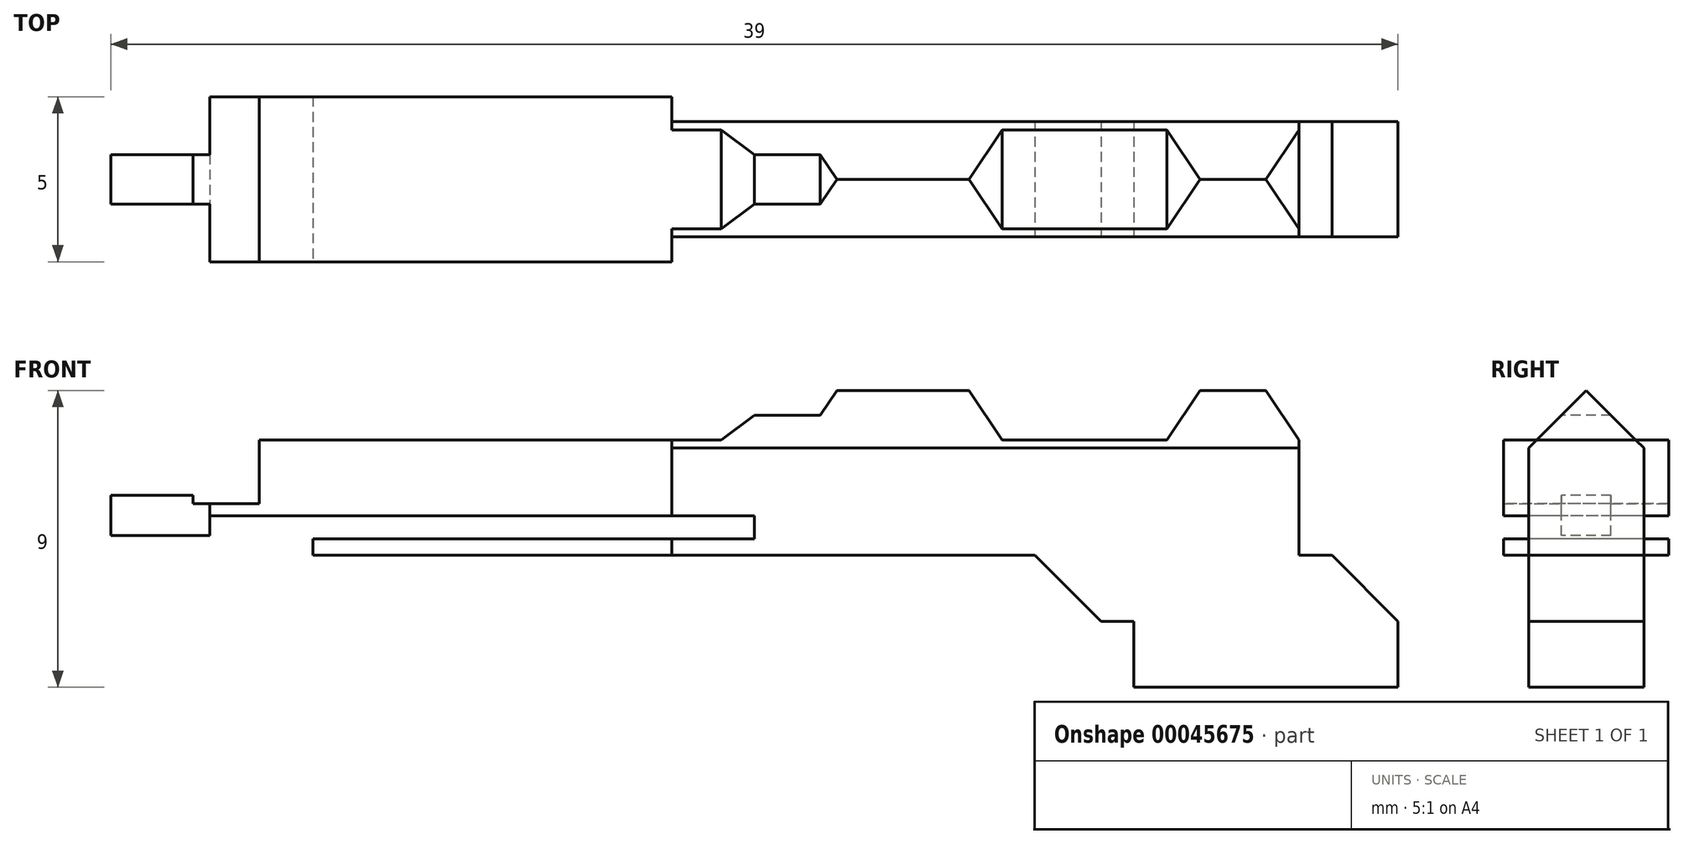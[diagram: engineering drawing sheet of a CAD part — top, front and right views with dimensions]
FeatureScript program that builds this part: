
annotation { "Feature Type Name" : "Feature", "Feature Type Description" : "" }
export const myFeature = defineFeature(function(context is Context, id is Id, definition is map)
    precondition{}
    {
        {
            var Q0;
            Q0=qCreatedBy(makeId("Top.planeOp"),FACE);
            var sketch = newSketch(context, id + "F0", { "sketchPlane" : qUnion([Q0])});
            skLineSegment(sketch, "E0.bottom", {"start": v(-9.8, 2.5) * mm, "end": v(4.2, 2.5) * mm});
            skLineSegment(sketch, "E0.top", {"start": v(-9.8, -2.5) * mm, "end": v(4.2, -2.5) * mm});
            skLineSegment(sketch, "E0.left", {"start": v(-9.8, 2.5) * mm, "end": v(-9.8, -2.5) * mm});
            skLineSegment(sketch, "E0.right", {"start": v(4.2, 2.5) * mm, "end": v(4.2, 1.75) * mm});
            skLineSegment(sketch, "E1.bottom", {"start": v(4.2, 1.75) * mm, "end": v(26.2, 1.75) * mm});
            skLineSegment(sketch, "E1.top", {"start": v(4.2, -1.75) * mm, "end": v(26.2, -1.75) * mm});
            skLineSegment(sketch, "E1.right", {"start": v(26.2, 1.75) * mm, "end": v(26.2, -1.75) * mm});
            skLineSegment(sketch, "E2.bottom", {"start": v(18.2, 1.75) * mm, "end": v(26.2, 1.75) * mm});
            skLineSegment(sketch, "E2.top", {"start": v(18.2, -1.75) * mm, "end": v(26.2, -1.75) * mm});
            skLineSegment(sketch, "E2.right", {"start": v(18.2, 1.75) * mm, "end": v(18.2, -1.75) * mm});
            skLineSegment(sketch, "E3.bottom", {"start": v(15.2, 1.75) * mm, "end": v(18.2, 1.75) * mm});
            skLineSegment(sketch, "E3.top", {"start": v(15.2, -1.75) * mm, "end": v(18.2, -1.75) * mm});
            skLineSegment(sketch, "E3.right", {"start": v(15.2, 1.75) * mm, "end": v(15.2, -1.75) * mm});
            skLineSegment(sketch, "E4.trimOffspring", {"start": v(4.2, -1.75) * mm, "end": v(4.2, -2.5) * mm});
            skLineSegment(sketch, "E5.bottom", {"start": v(15.2, 1.75) * mm, "end": v(17.2, 1.75) * mm});
            skLineSegment(sketch, "E5.top", {"start": v(15.2, -1.75) * mm, "end": v(17.2, -1.75) * mm});
            skLineSegment(sketch, "E5.right", {"start": v(17.2, 1.75) * mm, "end": v(17.2, -1.75) * mm});
            skLineSegment(sketch, "E6", {"start": v(-9.8, 0) * mm, "end": v(17.2, 0) * mm, "construction": true});
            skLineSegment(sketch, "E7.bottom", {"start": v(-9.8, 0.75) * mm, "end": v(-12.8, 0.75) * mm});
            skLineSegment(sketch, "E7.top", {"start": v(-9.8, -0.75) * mm, "end": v(-12.8, -0.75) * mm});
            skLineSegment(sketch, "E7.left", {"start": v(-9.8, 0.75) * mm, "end": v(-9.8, -0.75) * mm});
            skLineSegment(sketch, "E7.right", {"start": v(-12.8, 0.75) * mm, "end": v(-12.8, -0.75) * mm});
            skLineSegment(sketch, "E8", {"start": v(-12.8, 0) * mm, "end": v(-9.8, 0) * mm, "construction": true});
            skSolve(sketch);
        }
        {
            var Q0;
            Q0 = qSketchRegion(id + "F0", true);
            extrude(context, id + "F1", {"entities" : qUnion([Q0]), "oppositeDirection" : true, "depth" : 9 * mm});
        }
        {
            var Q0;
            Q0=makeQuery(id+"F1.opExtrude","SWEPT_FACE",FACE,{"disambiguationData":[OSD([sQuery(id+"F0.wireOp",EDGE,"E0.bottom")])]});
            cPlane(context, id + "F2", {"entities" : qUnion([Q0]), "cplaneType" : CPlaneType.OFFSET, "offset" : 0 * mm, "width" : 150 * mm, "height" : 150 * mm});
        }
        {
            var Q0;
            Q0=qCreatedBy(id+"F2.planeOp",FACE);
            var sketch = newSketch(context, id + "F3", { "sketchPlane" : qUnion([Q0])});
            skLineSegment(sketch, "E9.0.0", {"start": v(-26.2, 0) * mm, "end": v(-4.2, 0) * mm});
            skLineSegment(sketch, "E9.0.2", {"start": v(-4.2, -9) * mm, "end": v(-26.2, -9) * mm});
            skLineSegment(sketch, "E9.0.3", {"start": v(-26.2, -9) * mm, "end": v(-26.2, 0) * mm});
            skLineSegment(sketch, "E10.0.0", {"start": v(-4.2, 0) * mm, "end": v(9.8, 0) * mm});
            skLineSegment(sketch, "E10.0.2", {"start": v(9.8, -9) * mm, "end": v(-4.2, -9) * mm});
            skLineSegment(sketch, "E11.0.0", {"start": v(9.8, 0) * mm, "end": v(12.8, 0) * mm});
            skLineSegment(sketch, "E11.0.1", {"start": v(12.8, 0) * mm, "end": v(12.8, -9) * mm});
            skLineSegment(sketch, "E11.0.2", {"start": v(12.8, -9) * mm, "end": v(9.8, -9) * mm});
            skLineSegment(sketch, "E12", {"start": v(-24.2, 0) * mm, "end": v(-24.2, -9) * mm, "construction": true});
            skLineSegment(sketch, "E13", {"start": v(-23.2, 0) * mm, "end": v(-23.2, -9) * mm, "construction": true});
            skLineSegment(sketch, "E14", {"start": v(-22.2, 0) * mm, "end": v(-22.2, -9) * mm, "construction": true});
            skLineSegment(sketch, "E15", {"start": v(-20.2, 0) * mm, "end": v(-20.2, -9) * mm, "construction": true});
            skLineSegment(sketch, "E16", {"start": v(-19.2, 0) * mm, "end": v(-19.2, -9) * mm, "construction": true});
            skLineSegment(sketch, "E17", {"start": v(-18.2, 0) * mm, "end": v(-18.2, -9) * mm, "construction": true});
            skLineSegment(sketch, "E18", {"start": v(-18.2, -7) * mm, "end": v(-26.2, -7) * mm, "construction": true});
            skLineSegment(sketch, "E19", {"start": v(-18.2, -5) * mm, "end": v(-26.2, -5) * mm, "construction": true});
            skLineSegment(sketch, "E20", {"start": v(-18.2, -1.5) * mm, "end": v(-26.2, -1.5) * mm, "construction": true});
            skLineSegment(sketch, "E21", {"start": v(-26.2, -7) * mm, "end": v(-24.2, -5) * mm});
            skLineSegment(sketch, "E22", {"start": v(-24.2, -5) * mm, "end": v(-23.2, -5) * mm});
            skLineSegment(sketch, "E23", {"start": v(-23.2, -5) * mm, "end": v(-23.2, -1.5) * mm});
            skLineSegment(sketch, "E24", {"start": v(-23.2, -1.5) * mm, "end": v(-22.2, 0) * mm});
            skLineSegment(sketch, "E25", {"start": v(-20.2, 0) * mm, "end": v(-22.2, 0) * mm});
            skLineSegment(sketch, "E26", {"start": v(-20.2, 0) * mm, "end": v(-19.2, -1.5) * mm});
            skLineSegment(sketch, "E27", {"start": v(-19.2, -1.5) * mm, "end": v(-18.2, -1.5) * mm});
            skSolve(sketch);
        }
        {
            var Q0;
            Q0=qCreatedBy(id+"F2.planeOp",FACE);
            var sketch = newSketch(context, id + "F4", { "sketchPlane" : qUnion([Q0])});
            skLineSegment(sketch, "E28.0", {"start": v(-24.2, -5) * mm, "end": v(-23.2, -5) * mm});
            skLineSegment(sketch, "E29.0", {"start": v(-23.2, -5) * mm, "end": v(-23.2, -1.5) * mm});
            skLineSegment(sketch, "E30.0", {"start": v(-26.2, -7) * mm, "end": v(-24.2, -5) * mm});
            skLineSegment(sketch, "E31.0", {"start": v(-23.2, -1.5) * mm, "end": v(-22.2, 0) * mm});
            skLineSegment(sketch, "E32.0", {"start": v(-20.2, 0) * mm, "end": v(-22.2, 0) * mm});
            skLineSegment(sketch, "E33.0", {"start": v(-20.2, 0) * mm, "end": v(-19.2, -1.5) * mm});
            skLineSegment(sketch, "E34.0", {"start": v(-19.2, -1.5) * mm, "end": v(-18.2, -1.5) * mm});
            skLineSegment(sketch, "E35", {"start": v(-18.2, -1.5) * mm, "end": v(-18.2, 0) * mm});
            skLineSegment(sketch, "E36", {"start": v(-18.2, 0) * mm, "end": v(-20.2, 0) * mm});
            skLineSegment(sketch, "E37.0", {"start": v(-26.2, -7) * mm, "end": v(-26.2, 0) * mm});
            skLineSegment(sketch, "E38.0", {"start": v(-26.2, 0) * mm, "end": v(-22.2, 0) * mm});
            skPoint(sketch, "E39.orphan", {"position": v(-4.2, 0) * mm});
            skLineSegment(sketch, "E40.trimOffspring", {"start": v(-20.2, 0) * mm, "end": v(-18.2, 0) * mm});
            skPoint(sketch, "E41.orphan", {"position": v(-26.2, -9) * mm});
            skSolve(sketch);
        }
        {
            var Q0;
            Q0 = qSketchRegion(id + "F4", true);
            extrude(context, id + "F5", {"entities" : qUnion([Q0]), "operationType" : NewBodyOperationType.REMOVE, "oppositeDirection" : true, "depth" : 25 * mm});
        }
        {
            var Q0;
            Q0=makeQuery(id+"F1.opExtrude","SWEPT_FACE",FACE,{"disambiguationData":[OSD([sQuery(id+"F0.wireOp",EDGE,"E1.top"),sQuery(id+"F0.wireOp",EDGE,"E2.top"),sQuery(id+"F0.wireOp",EDGE,"E3.top"),sQuery(id+"F0.wireOp",EDGE,"E5.top")])]});
            var sketch = newSketch(context, id + "F6", { "sketchPlane" : qUnion([Q0])});
            skLineSegment(sketch, "E42.0.0", {"start": v(20.2, 0) * mm, "end": v(19.2, -1.5) * mm, "construction": true});
            skLineSegment(sketch, "E42.0.1", {"start": v(19.2, -1.5) * mm, "end": v(18.2, -1.5) * mm, "construction": true});
            skLineSegment(sketch, "E42.0.2", {"start": v(18.2, -1.5) * mm, "end": v(18.2, 0) * mm, "construction": true});
            skLineSegment(sketch, "E42.0.3", {"start": v(18.2, 0) * mm, "end": v(4.2, 0) * mm, "construction": true});
            skLineSegment(sketch, "E42.0.4", {"start": v(4.2, 0) * mm, "end": v(4.2, -9) * mm, "construction": true});
            skLineSegment(sketch, "E42.0.5", {"start": v(4.2, -9) * mm, "end": v(26.2, -9) * mm, "construction": true});
            skLineSegment(sketch, "E42.0.6", {"start": v(26.2, -9) * mm, "end": v(26.2, -7) * mm, "construction": true});
            skLineSegment(sketch, "E42.0.7", {"start": v(26.2, -7) * mm, "end": v(24.2, -5) * mm, "construction": true});
            skLineSegment(sketch, "E42.0.8", {"start": v(24.2, -5) * mm, "end": v(23.2, -5) * mm, "construction": true});
            skLineSegment(sketch, "E42.0.9", {"start": v(23.2, -5) * mm, "end": v(23.2, -1.5) * mm, "construction": true});
            skLineSegment(sketch, "E42.0.10", {"start": v(23.2, -1.5) * mm, "end": v(22.2, 0) * mm, "construction": true});
            skLineSegment(sketch, "E42.0.11", {"start": v(22.2, 0) * mm, "end": v(20.2, 0) * mm, "construction": true});
            skLineSegment(sketch, "E43", {"start": v(18.2, 0) * mm, "end": v(18.2, -9) * mm, "construction": true});
            skLineSegment(sketch, "E44", {"start": v(17.2, 0) * mm, "end": v(17.2, -9) * mm, "construction": true});
            skLineSegment(sketch, "E45", {"start": v(15.2, 0) * mm, "end": v(15.2, -9) * mm, "construction": true});
            skLineSegment(sketch, "E46", {"start": v(14.2, 0) * mm, "end": v(14.2, -9) * mm, "construction": true});
            skLineSegment(sketch, "E47", {"start": v(13.2, 0) * mm, "end": v(13.2, -9) * mm, "construction": true});
            skLineSegment(sketch, "E48", {"start": v(9.2, 0) * mm, "end": v(9.2, -9) * mm, "construction": true});
            skLineSegment(sketch, "E49", {"start": v(5.7, 0) * mm, "end": v(5.7, -9) * mm, "construction": true});
            skLineSegment(sketch, "E50", {"start": v(6.7, 0) * mm, "end": v(6.7, -9) * mm, "construction": true});
            skLineSegment(sketch, "E51", {"start": v(8.7, 0) * mm, "end": v(8.7, -9) * mm, "construction": true});
            skLineSegment(sketch, "E52", {"start": v(18.2, -1.5) * mm, "end": v(4.2, -1.5) * mm, "construction": true});
            skLineSegment(sketch, "E53", {"start": v(18.2, -3.5) * mm, "end": v(4.2, -3.5) * mm, "construction": true});
            skLineSegment(sketch, "E54", {"start": v(18.2, -5) * mm, "end": v(4.2, -5) * mm, "construction": true});
            skLineSegment(sketch, "E55", {"start": v(18.2, -7) * mm, "end": v(4.2, -7) * mm, "construction": true});
            skLineSegment(sketch, "E56", {"start": v(18.2, -9) * mm, "end": v(18.2, -7) * mm});
            skLineSegment(sketch, "E57", {"start": v(18.2, -7) * mm, "end": v(17.2, -7) * mm});
            skLineSegment(sketch, "E58", {"start": v(17.2, -7) * mm, "end": v(15.2, -5) * mm});
            skLineSegment(sketch, "E59", {"start": v(4.2, -5) * mm, "end": v(15.2, -5) * mm});
            skLineSegment(sketch, "E60", {"start": v(4.2, -5) * mm, "end": v(4.2, -9) * mm});
            skLineSegment(sketch, "E61", {"start": v(4.2, -9) * mm, "end": v(18.2, -9) * mm});
            skLineSegment(sketch, "E62", {"start": v(18.2, -1.5) * mm, "end": v(15.2, -1.5) * mm});
            skLineSegment(sketch, "E63", {"start": v(14.2, -1.5) * mm, "end": v(15.2, -1.5) * mm});
            skLineSegment(sketch, "E64", {"start": v(14.2, -1.5) * mm, "end": v(13.2, 0) * mm});
            skLineSegment(sketch, "E65", {"start": v(13.2, 0) * mm, "end": v(9.2, 0) * mm});
            skLineSegment(sketch, "E66", {"start": v(4.2, 0) * mm, "end": v(18.2, 0) * mm});
            skLineSegment(sketch, "E67", {"start": v(18.2, 0) * mm, "end": v(18.2, -1.5) * mm});
            skLineSegment(sketch, "E68", {"start": v(4.2, -1.5) * mm, "end": v(4.2, -2.5) * mm});
            skPoint(sketch, "E69.startSnap0", {"position": v(4.2, -2.5) * mm});
            skPoint(sketch, "E70.start.orphan", {"position": v(5.7, -2.5) * mm});
            skLineSegment(sketch, "E71", {"start": v(4.2, -1.5) * mm, "end": v(4.2, 0) * mm});
            skLineSegment(sketch, "E72", {"start": v(4.2, -0.75) * mm, "end": v(18.2, -0.75) * mm, "construction": true});
            skLineSegment(sketch, "E73", {"start": v(9.2, 0) * mm, "end": v(8.7, -0.75) * mm});
            skLineSegment(sketch, "E74", {"start": v(8.7, -0.75) * mm, "end": v(6.7, -0.75) * mm});
            skLineSegment(sketch, "E75", {"start": v(6.7, -0.75) * mm, "end": v(5.7, -1.5) * mm});
            skLineSegment(sketch, "E76", {"start": v(5.7, -1.5) * mm, "end": v(4.2, -1.5) * mm});
            skSolve(sketch);
        }
        {
            var Q0;
            Q0 = qSketchRegion(id + "F6", true);
            extrude(context, id + "F7", {"entities" : qUnion([Q0]), "operationType" : NewBodyOperationType.REMOVE, "oppositeDirection" : true, "depth" : 25 * mm});
        }
        {
            var Q0;
            Q0=makeQuery(id+"F1.opExtrude","SWEPT_FACE",FACE,{"disambiguationData":[OSD([sQuery(id+"F0.wireOp",EDGE,"E0.top")])]});
            var sketch = newSketch(context, id + "F8", { "sketchPlane" : qUnion([Q0])});
            skLineSegment(sketch, "E77", {"start": v(-0.8, 0) * mm, "end": v(-0.8, -9) * mm, "construction": true});
            skLineSegment(sketch, "E78", {"start": v(-3.8, 0) * mm, "end": v(-3.8, -9) * mm, "construction": true});
            skLineSegment(sketch, "E79", {"start": v(-8.3, 0) * mm, "end": v(-8.3, -9) * mm, "construction": true});
            skLineSegment(sketch, "E80.0.0", {"start": v(-9.8, 0) * mm, "end": v(-12.8, 0) * mm, "construction": true});
            skLineSegment(sketch, "E80.0.1", {"start": v(-12.8, 0) * mm, "end": v(-12.8, -9) * mm, "construction": true});
            skLineSegment(sketch, "E80.0.2", {"start": v(-12.8, -9) * mm, "end": v(-9.8, -9) * mm, "construction": true});
            skLineSegment(sketch, "E80.0.3", {"start": v(-9.8, -9) * mm, "end": v(-9.8, 0) * mm, "construction": true});
            skLineSegment(sketch, "E81", {"start": v(-10.3, 0) * mm, "end": v(-10.3, -9) * mm, "construction": true});
            skLineSegment(sketch, "E82.0.0", {"start": v(4.2, 0) * mm, "end": v(-9.8, 0) * mm, "construction": true});
            skLineSegment(sketch, "E82.0.1", {"start": v(-9.8, 0) * mm, "end": v(-9.8, -9) * mm, "construction": true});
            skLineSegment(sketch, "E82.0.2", {"start": v(-9.8, -9) * mm, "end": v(4.2, -9) * mm, "construction": true});
            skLineSegment(sketch, "E82.0.3", {"start": v(4.2, -9) * mm, "end": v(4.2, 0) * mm, "construction": true});
            skLineSegment(sketch, "E83", {"start": v(4.2, -1.5) * mm, "end": v(-8.3, -1.5) * mm, "construction": true});
            skLineSegment(sketch, "E84", {"start": v(4.2, -5) * mm, "end": v(-10.3, -5) * mm, "construction": true});
            skLineSegment(sketch, "E85", {"start": v(4.2, -9) * mm, "end": v(4.2, -5) * mm});
            skLineSegment(sketch, "E86", {"start": v(4.2, -5) * mm, "end": v(-10.3, -5) * mm});
            skLineSegment(sketch, "E87", {"start": v(-10.3, -5) * mm, "end": v(-12.8, -5) * mm});
            skLineSegment(sketch, "E88", {"start": v(-12.8, -5) * mm, "end": v(-12.8, -9) * mm});
            skLineSegment(sketch, "E89", {"start": v(-12.8, -9) * mm, "end": v(4.2, -9) * mm});
            skLineSegment(sketch, "E90", {"start": v(4.2, 0) * mm, "end": v(4.2, -1.5) * mm});
            skLineSegment(sketch, "E91", {"start": v(4.2, -1.5) * mm, "end": v(-8.3, -1.5) * mm});
            skLineSegment(sketch, "E92", {"start": v(-8.3, -1.5) * mm, "end": v(-8.3, -3.43) * mm});
            skLineSegment(sketch, "E93", {"start": v(-8.3, -3.43) * mm, "end": v(-10.3, -3.43) * mm});
            skLineSegment(sketch, "E94", {"start": v(-10.3, -3.43) * mm, "end": v(-10.3, -3.18) * mm});
            skLineSegment(sketch, "E95", {"start": v(-10.3, -3.18) * mm, "end": v(-12.8, -3.18) * mm});
            skLineSegment(sketch, "E96", {"start": v(-12.8, 0) * mm, "end": v(-12.8, -3.18) * mm});
            skLineSegment(sketch, "E97", {"start": v(-12.8, 0) * mm, "end": v(4.2, 0) * mm});
            skSolve(sketch);
        }
        {
            var Q0;
            Q0 = qSketchRegion(id + "F8", true);
            extrude(context, id + "F9", {"entities" : qUnion([Q0]), "operationType" : NewBodyOperationType.REMOVE, "oppositeDirection" : true, "depth" : 25 * mm});
        }
        {
            var Q0;
            Q0=makeQuery(id+"F1.opExtrude","SWEPT_FACE",FACE,{"disambiguationData":[OSD([sQuery(id+"F0.wireOp",EDGE,"E0.top")])]});
            var sketch = newSketch(context, id + "F10", { "sketchPlane" : qUnion([Q0])});
            skLineSegment(sketch, "E98.0.0", {"start": v(-9.8, -5) * mm, "end": v(4.2, -5) * mm, "construction": true});
            skLineSegment(sketch, "E98.0.1", {"start": v(4.2, -5) * mm, "end": v(4.2, -1.5) * mm, "construction": true});
            skLineSegment(sketch, "E98.0.2", {"start": v(4.2, -1.5) * mm, "end": v(-8.3, -1.5) * mm, "construction": true});
            skLineSegment(sketch, "E98.0.3", {"start": v(-8.3, -1.5) * mm, "end": v(-8.3, -3.43) * mm, "construction": true});
            skLineSegment(sketch, "E98.0.4", {"start": v(-8.3, -3.43) * mm, "end": v(-9.8, -3.43) * mm, "construction": true});
            skLineSegment(sketch, "E98.0.5", {"start": v(-9.8, -3.43) * mm, "end": v(-9.8, -5) * mm, "construction": true});
            skLineSegment(sketch, "E99.0.0", {"start": v(13.2, 0) * mm, "end": v(9.2, 0) * mm, "construction": true});
            skLineSegment(sketch, "E99.0.1", {"start": v(9.2, 0) * mm, "end": v(8.7, -0.75) * mm, "construction": true});
            skLineSegment(sketch, "E99.0.2", {"start": v(8.7, -0.75) * mm, "end": v(6.7, -0.75) * mm, "construction": true});
            skLineSegment(sketch, "E99.0.3", {"start": v(6.7, -0.75) * mm, "end": v(5.7, -1.5) * mm, "construction": true});
            skLineSegment(sketch, "E99.0.4", {"start": v(5.7, -1.5) * mm, "end": v(4.2, -1.5) * mm, "construction": true});
            skLineSegment(sketch, "E99.0.5", {"start": v(4.2, -1.5) * mm, "end": v(4.2, -5) * mm, "construction": true});
            skLineSegment(sketch, "E99.0.6", {"start": v(4.2, -5) * mm, "end": v(15.2, -5) * mm, "construction": true});
            skLineSegment(sketch, "E99.0.7", {"start": v(15.2, -5) * mm, "end": v(17.2, -7) * mm, "construction": true});
            skLineSegment(sketch, "E99.0.8", {"start": v(17.2, -7) * mm, "end": v(18.2, -7) * mm, "construction": true});
            skLineSegment(sketch, "E99.0.9", {"start": v(18.2, -7) * mm, "end": v(18.2, -9) * mm, "construction": true});
            skLineSegment(sketch, "E99.0.10", {"start": v(18.2, -9) * mm, "end": v(26.2, -9) * mm, "construction": true});
            skLineSegment(sketch, "E99.0.11", {"start": v(26.2, -9) * mm, "end": v(26.2, -7) * mm, "construction": true});
            skLineSegment(sketch, "E99.0.12", {"start": v(26.2, -7) * mm, "end": v(24.2, -5) * mm, "construction": true});
            skLineSegment(sketch, "E99.0.13", {"start": v(24.2, -5) * mm, "end": v(23.2, -5) * mm, "construction": true});
            skLineSegment(sketch, "E99.0.14", {"start": v(23.2, -5) * mm, "end": v(23.2, -1.5) * mm, "construction": true});
            skLineSegment(sketch, "E99.0.15", {"start": v(23.2, -1.5) * mm, "end": v(22.2, 0) * mm, "construction": true});
            skLineSegment(sketch, "E99.0.16", {"start": v(22.2, 0) * mm, "end": v(20.2, 0) * mm, "construction": true});
            skLineSegment(sketch, "E99.0.17", {"start": v(20.2, 0) * mm, "end": v(19.2, -1.5) * mm, "construction": true});
            skLineSegment(sketch, "E99.0.18", {"start": v(19.2, -1.5) * mm, "end": v(14.2, -1.5) * mm, "construction": true});
            skLineSegment(sketch, "E99.0.19", {"start": v(14.2, -1.5) * mm, "end": v(13.2, 0) * mm, "construction": true});
            skLineSegment(sketch, "E100.0.0", {"start": v(-12.8, -3.18) * mm, "end": v(-12.8, -5) * mm, "construction": true});
            skLineSegment(sketch, "E100.0.1", {"start": v(-12.8, -5) * mm, "end": v(-9.8, -5) * mm, "construction": true});
            skLineSegment(sketch, "E100.0.2", {"start": v(-9.8, -5) * mm, "end": v(-9.8, -3.43) * mm, "construction": true});
            skLineSegment(sketch, "E100.0.3", {"start": v(-9.8, -3.43) * mm, "end": v(-10.3, -3.43) * mm, "construction": true});
            skLineSegment(sketch, "E100.0.4", {"start": v(-10.3, -3.43) * mm, "end": v(-10.3, -3.18) * mm, "construction": true});
            skLineSegment(sketch, "E100.0.5", {"start": v(-10.3, -3.18) * mm, "end": v(-12.8, -3.18) * mm, "construction": true});
            skLineSegment(sketch, "E101", {"start": v(-6.67, -5) * mm, "end": v(-6.67, -4.5) * mm});
            skLineSegment(sketch, "E102", {"start": v(-6.67, -4.5) * mm, "end": v(6.7, -4.5) * mm});
            skLineSegment(sketch, "E103", {"start": v(6.7, -4.5) * mm, "end": v(6.7, -3.8) * mm});
            skLineSegment(sketch, "E104", {"start": v(6.7, -3.8) * mm, "end": v(-9.8, -3.8) * mm});
            skLineSegment(sketch, "E105", {"start": v(-9.8, -3.8) * mm, "end": v(-9.8, -5) * mm});
            skLineSegment(sketch, "E106", {"start": v(-9.8, -5) * mm, "end": v(-6.67, -5) * mm});
            skLineSegment(sketch, "E107", {"start": v(-9.8, -3.8) * mm, "end": v(-9.8, -4.4) * mm});
            skLineSegment(sketch, "E108", {"start": v(-9.8, -4.4) * mm, "end": v(-12.8, -4.4) * mm});
            skLineSegment(sketch, "E109", {"start": v(-12.8, -4.4) * mm, "end": v(-12.8, -5) * mm});
            skLineSegment(sketch, "E110", {"start": v(-12.8, -5) * mm, "end": v(-9.8, -5) * mm});
            skSolve(sketch);
        }
        {
            var Q0;
            Q0 = qSketchRegion(id + "F10", true);
            extrude(context, id + "F11", {"entities" : qUnion([Q0]), "operationType" : NewBodyOperationType.REMOVE, "oppositeDirection" : true, "depth" : 25 * mm});
        }
        {
            var Q0;
            {var subQ0=sQuery(id+"F0.wireOp",EDGE,"E1.top");var subQ1=sQuery(id+"F0.wireOp",EDGE,"E2.top");var subQ2=sQuery(id+"F0.wireOp",EDGE,"E3.top");var subQ3=sQuery(id+"F0.wireOp",EDGE,"E5.top");Q0=makeQuery(id+"F5.boolean.opBoolean","SPLIT",EDGE,{"disambiguationData":[TD([makeQuery(id+"F5.opExtrude","SWEPT_FACE",FACE,{"disambiguationData":[OSD([sQuery(id+"F4.wireOp",EDGE,"E31.0")])]})])],"derivedFrom":makeQuery(id+"F1.opExtrude","CAP_EDGE",EDGE,{"disambiguationData":[OSD([subQ0,subQ1,subQ2,subQ3])],"isStart":true})});}
            chamfer(context, id + "F12", {"entities" : qUnion([Q0]), "chamferType" : ChamferType.OFFSET_ANGLE, "width" : 1.75 * mm, "oppositeDirection" : false, "angle" : 45 * degree});
        }
        {
            var Q0;
            {var subQ0=sQuery(id+"F0.wireOp",EDGE,"E1.bottom");var subQ1=sQuery(id+"F0.wireOp",EDGE,"E2.bottom");var subQ2=sQuery(id+"F0.wireOp",EDGE,"E3.bottom");var subQ3=sQuery(id+"F0.wireOp",EDGE,"E5.bottom");Q0=makeQuery(id+"F5.boolean.opBoolean","SPLIT",EDGE,{"disambiguationData":[TD([makeQuery(id+"F5.opExtrude","SWEPT_FACE",FACE,{"disambiguationData":[OSD([sQuery(id+"F4.wireOp",EDGE,"E31.0")])]})])],"derivedFrom":makeQuery(id+"F1.opExtrude","CAP_EDGE",EDGE,{"disambiguationData":[OSD([subQ0,subQ1,subQ2,subQ3])],"isStart":true})});}
            chamfer(context, id + "F13", {"entities" : qUnion([Q0]), "chamferType" : ChamferType.OFFSET_ANGLE, "width" : 1.75 * mm, "oppositeDirection" : false, "angle" : 45 * degree});
        }
    });
